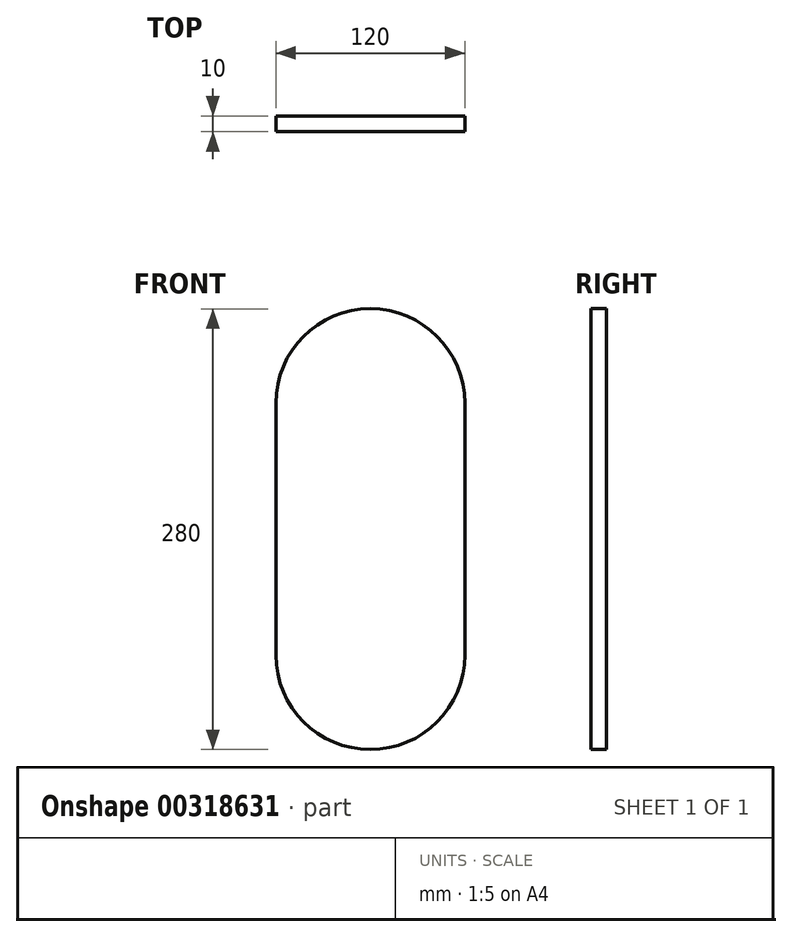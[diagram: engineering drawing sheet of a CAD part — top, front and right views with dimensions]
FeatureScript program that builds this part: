
annotation { "Feature Type Name" : "Feature", "Feature Type Description" : "" }
export const myFeature = defineFeature(function(context is Context, id is Id, definition is map)
    precondition{}
    {
        {
            var Q0;
            Q0=qCreatedBy(makeId("Front.planeOp"),FACE);
            var sketch = newSketch(context, id + "F0", { "sketchPlane" : qUnion([Q0])});
            skLineSegment(sketch, "E0", {"start": v(19.91, -60.72) * mm, "end": v(19.91, 99.28) * mm});
            skLineSegment(sketch, "E1.MirrorCS", {"start": v(-100.09, -60.72) * mm, "end": v(-100.09, 99.28) * mm});
            skArc(sketch, "E2", {"start": v(19.91, 99.28) * mm, "mid": v(-40.09, 159.28) * mm, "end": v(-100.09, 99.28) * mm});
            skArc(sketch, "E3", {"start": v(-100.09, -60.72) * mm, "mid": v(-40.09, -120.72) * mm, "end": v(19.91, -60.72) * mm});
            skSolve(sketch);
        }
        {
            var Q0;
            Q0=makeQuery(id+"F0.imprint","IMPRINT",FACE,{"disambiguationData":[TD([[makeQuery(id+"F0.imprint","IMPRINT",EDGE,{"derivedFrom":sQuery(id+"F0.wireOp",EDGE,"E0")}),1.0]])]});
            extrude(context, id + "F1", {"entities" : qUnion([Q0]), "depth" : 10 * mm});
        }
    });
